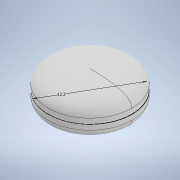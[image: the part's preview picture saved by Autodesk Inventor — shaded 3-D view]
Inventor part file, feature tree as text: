
AUTODESK INVENTOR PART (.ipt)
format: ipt  version: 2020 (Build 240168000, 168)  size: 240,640 bytes
history: native  units: mm
features: sketch x2, revolve x1, mirror x1
ambient origin geometry x8: Origin, YZ Plane, XZ Plane, XY Plane, X Axis, Y Axis, Z Axis, Center Point
bodies: Solid1 (feature_tree)
feature tree (4):
  sketch  "Sketch1"  dims[d0=12.2mm d1=2.7mm]
  revolve  "Revolution1"  [1 undecoded]
  mirror  "Mirror1"
  sketch  "Sketch2"  dims[d2=2.7mm d3=90.0deg]
note: 1 required parameter value undecoded (feature->parameter linkage not recoverable at this tier; creation-order binding heuristic only, values carry confidence <= 0.55)
